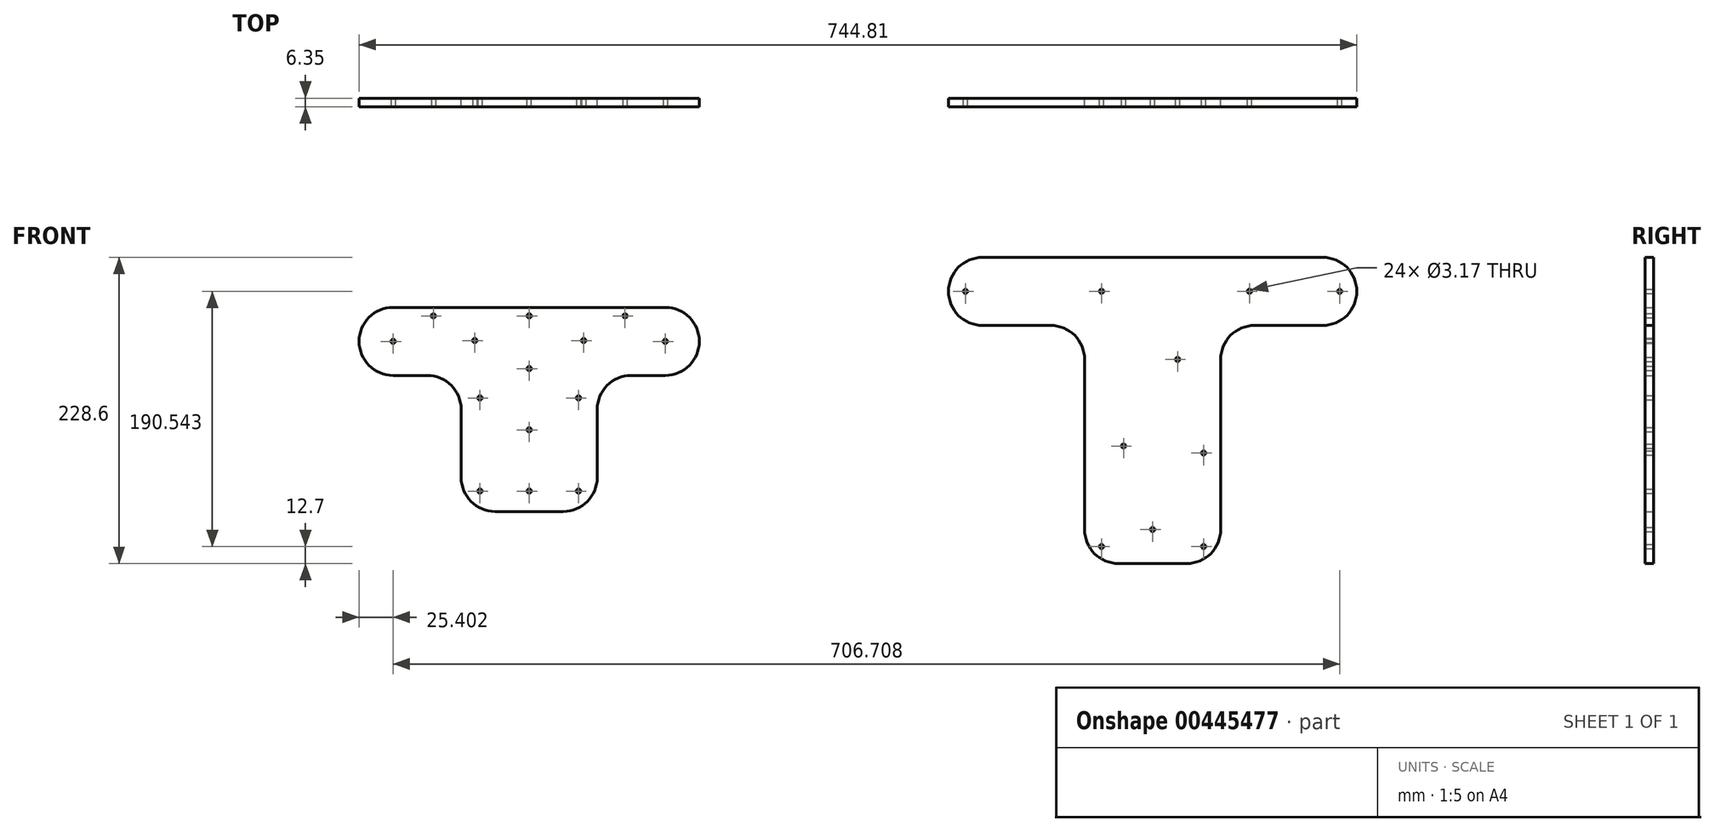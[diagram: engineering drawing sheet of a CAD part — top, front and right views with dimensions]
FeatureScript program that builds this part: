
annotation { "Feature Type Name" : "Feature", "Feature Type Description" : "" }
export const myFeature = defineFeature(function(context is Context, id is Id, definition is map)
    precondition{}
    {
        {
            var Q0;
            Q0=qCreatedBy(makeId("Front.planeOp"),FACE);
            var sketch = newSketch(context, id + "F0", { "sketchPlane" : qUnion([Q0])});
            skLineSegment(sketch, "E0.bottom", {"start": v(-50.8, 114.3) * mm, "end": v(50.8, 114.3) * mm});
            skLineSegment(sketch, "E0.top", {"start": v(-50.8, -114.3) * mm, "end": v(50.8, -114.3) * mm});
            skLineSegment(sketch, "E0.left", {"start": v(-50.8, 114.3) * mm, "end": v(-50.8, -114.3) * mm});
            skLineSegment(sketch, "E0.right", {"start": v(50.8, 114.3) * mm, "end": v(50.8, -114.3) * mm});
            skPoint(sketch, "E0.middle", {"position": v(0, 0) * mm});
            skCircle(sketch, "E1", {"center": v(0, -88.9) * mm, "radius": 15.24 * mm, "construction": true});
            skCircle(sketch, "E2", {"center": v(-21.7, -26.53) * mm, "radius": 50.8 * mm, "construction": true});
            skCircle(sketch, "E3", {"center": v(-21.7, -26.53) * mm, "radius": 25.4 * mm, "construction": true});
            skCircle(sketch, "E4", {"center": v(18.66, 38.1) * mm, "radius": 50.8 * mm, "construction": true});
            skCircle(sketch, "E5", {"center": v(18.66, 38.1) * mm, "radius": 25.4 * mm, "construction": true});
            skCircle(sketch, "E6", {"center": v(-38.1, 88.94) * mm, "radius": 50.8 * mm, "construction": true});
            skLineSegment(sketch, "E7", {"start": v(-50.8, 114.3) * mm, "end": v(-152.4, 114.3) * mm});
            skLineSegment(sketch, "E8", {"start": v(-152.4, 114.3) * mm, "end": v(-152.4, 63.5) * mm});
            skLineSegment(sketch, "E9", {"start": v(-152.4, 63.5) * mm, "end": v(-50.8, 63.5) * mm});
            skLineSegment(sketch, "E10", {"start": v(50.8, 63.5) * mm, "end": v(152.4, 63.5) * mm});
            skLineSegment(sketch, "E11", {"start": v(152.4, 63.5) * mm, "end": v(152.4, 114.3) * mm});
            skLineSegment(sketch, "E12", {"start": v(152.4, 114.3) * mm, "end": v(50.8, 114.3) * mm});
            skPoint(sketch, "E13", {"position": v(-152.4, 88.9) * mm});
            skCircle(sketch, "E14", {"center": v(-139.7, 88.9) * mm, "radius": 50.8 * mm, "construction": true});
            skLineSegment(sketch, "E15", {"start": v(-139.7, 88.9) * mm, "end": v(-152.4, 88.9) * mm});
            skLineSegment(sketch, "E16", {"start": v(152.4, 88.9) * mm, "end": v(139.7, 88.9) * mm});
            skPoint(sketch, "E16.endSnap0", {"position": v(152.4, 88.9) * mm});
            skCircle(sketch, "E17", {"center": v(139.7, 88.9) * mm, "radius": 50.8 * mm, "construction": true});
            skCircle(sketch, "E18", {"center": v(-139.7, 88.9) * mm, "radius": 1.59 * mm});
            skCircle(sketch, "E19", {"center": v(-38.1, 88.94) * mm, "radius": 1.59 * mm});
            skCircle(sketch, "E20", {"center": v(139.7, 88.9) * mm, "radius": 1.59 * mm});
            skCircle(sketch, "E21", {"center": v(18.66, 38.1) * mm, "radius": 1.59 * mm});
            skCircle(sketch, "E22", {"center": v(-21.7, -26.53) * mm, "radius": 1.59 * mm});
            skCircle(sketch, "E23", {"center": v(0, -88.9) * mm, "radius": 1.59 * mm});
            skLineSegment(sketch, "E24", {"start": v(-516.2, -75.44) * mm, "end": v(-414.6, -75.44) * mm});
            skLineSegment(sketch, "E25", {"start": v(-414.6, -75.44) * mm, "end": v(-414.6, 26.16) * mm});
            skLineSegment(sketch, "E26", {"start": v(-414.6, 26.16) * mm, "end": v(-338.4, 26.16) * mm});
            skLineSegment(sketch, "E27", {"start": v(-338.4, 26.16) * mm, "end": v(-338.4, 76.96) * mm});
            skLineSegment(sketch, "E28", {"start": v(-338.4, 76.96) * mm, "end": v(-592.4, 76.96) * mm});
            skLineSegment(sketch, "E29", {"start": v(-592.4, 76.96) * mm, "end": v(-592.4, 26.16) * mm});
            skLineSegment(sketch, "E30", {"start": v(-592.4, 26.16) * mm, "end": v(-516.2, 26.16) * mm});
            skLineSegment(sketch, "E31", {"start": v(-516.2, 26.16) * mm, "end": v(-516.2, -75.44) * mm});
            skCircle(sketch, "E32", {"center": v(-465.4, -60.2) * mm, "radius": 1.59 * mm});
            skPoint(sketch, "E32.centerSnap0", {"position": v(-465.4, -75.44) * mm});
            skLineSegment(sketch, "E33", {"start": v(-50.8, -114.3) * mm, "end": v(-38.1, -114.3) * mm});
            skLineSegment(sketch, "E34", {"start": v(-38.1, -114.3) * mm, "end": v(-38.1, -101.6) * mm});
            skCircle(sketch, "E35", {"center": v(-38.1, -101.6) * mm, "radius": 1.59 * mm});
            skLineSegment(sketch, "E36", {"start": v(50.8, -114.3) * mm, "end": v(38.1, -114.3) * mm});
            skLineSegment(sketch, "E37", {"start": v(38.1, -114.3) * mm, "end": v(38.1, -101.6) * mm});
            skCircle(sketch, "E38", {"center": v(38.1, -101.6) * mm, "radius": 1.59 * mm});
            skLineSegment(sketch, "E39", {"start": v(38.1, -31.75) * mm, "end": v(50.8, -31.75) * mm});
            skCircle(sketch, "E40", {"center": v(38.1, -31.75) * mm, "radius": 1.59 * mm});
            skLineSegment(sketch, "E41", {"start": v(-38.1, 88.94) * mm, "end": v(72.35, 88.94) * mm});
            skLineSegment(sketch, "E42", {"start": v(72.35, 88.94) * mm, "end": v(72.35, 114.3) * mm});
            skCircle(sketch, "E43", {"center": v(72.35, 88.94) * mm, "radius": 1.59 * mm});
            skSolve(sketch);
        }
        {
            var Q0;
            Q0 = qSketchRegion(id + "F0", true);
            extrude(context, id + "F1", {"entities" : qUnion([Q0]), "depth" : 6.35 * mm});
        }
        {
            var Q0;
            Q0=makeQuery(id+"F1.opExtrude","SWEPT_EDGE",EDGE,{"disambiguationData":[OSD([sQuery(id+"F0.wireOp",EDGE,"E0.left"),sQuery(id+"F0.wireOp",EDGE,"E9")])]});
            var Q1;
            Q1=makeQuery(id+"F1.opExtrude","SWEPT_EDGE",EDGE,{"disambiguationData":[OSD([sQuery(id+"F0.wireOp",EDGE,"E0.right"),sQuery(id+"F0.wireOp",EDGE,"E10")])]});
            var Q2;
            Q2=makeQuery(id+"F1.opExtrude","SWEPT_EDGE",EDGE,{"disambiguationData":[OSD([sQuery(id+"F0.wireOp",EDGE,"E10"),sQuery(id+"F0.wireOp",EDGE,"E11")])]});
            var Q3;
            Q3=makeQuery(id+"F1.opExtrude","SWEPT_EDGE",EDGE,{"disambiguationData":[OSD([sQuery(id+"F0.wireOp",EDGE,"E11"),sQuery(id+"F0.wireOp",EDGE,"E12")])]});
            var Q4;
            Q4=makeQuery(id+"F1.opExtrude","SWEPT_EDGE",EDGE,{"disambiguationData":[OSD([sQuery(id+"F0.wireOp",EDGE,"E0.top"),sQuery(id+"F0.wireOp",EDGE,"E0.right")])]});
            var Q5;
            Q5=makeQuery(id+"F1.opExtrude","SWEPT_EDGE",EDGE,{"disambiguationData":[OSD([sQuery(id+"F0.wireOp",EDGE,"E0.top"),sQuery(id+"F0.wireOp",EDGE,"E0.left")])]});
            var Q6;
            Q6=makeQuery(id+"F1.opExtrude","SWEPT_EDGE",EDGE,{"disambiguationData":[OSD([sQuery(id+"F0.wireOp",EDGE,"E8"),sQuery(id+"F0.wireOp",EDGE,"E9")])]});
            var Q7;
            Q7=makeQuery(id+"F1.opExtrude","SWEPT_EDGE",EDGE,{"disambiguationData":[OSD([sQuery(id+"F0.wireOp",EDGE,"E7"),sQuery(id+"F0.wireOp",EDGE,"E8")])]});
            fillet(context, id + "F2", {"entities" : qUnion([Q0, Q1, Q2, Q3, Q4, Q5, Q6, Q7]), "radius" : 25.4 * mm, "tangentPropagation" : true, "allowEdgeOverflow" : false});
        }
        {
            var Q0;
            Q0=makeQuery(id+"F1.opExtrude","SWEPT_EDGE",EDGE,{"disambiguationData":[OSD([sQuery(id+"F0.wireOp",EDGE,"E29"),sQuery(id+"F0.wireOp",EDGE,"E30")])]});
            var Q1;
            Q1=makeQuery(id+"F1.opExtrude","SWEPT_EDGE",EDGE,{"disambiguationData":[OSD([sQuery(id+"F0.wireOp",EDGE,"E30"),sQuery(id+"F0.wireOp",EDGE,"E31")])]});
            var Q2;
            Q2=makeQuery(id+"F1.opExtrude","SWEPT_EDGE",EDGE,{"disambiguationData":[OSD([sQuery(id+"F0.wireOp",EDGE,"E24"),sQuery(id+"F0.wireOp",EDGE,"E31")])]});
            var Q3;
            Q3=makeQuery(id+"F1.opExtrude","SWEPT_EDGE",EDGE,{"disambiguationData":[OSD([sQuery(id+"F0.wireOp",EDGE,"E25"),sQuery(id+"F0.wireOp",EDGE,"E26")])]});
            var Q4;
            Q4=makeQuery(id+"F1.opExtrude","SWEPT_EDGE",EDGE,{"disambiguationData":[OSD([sQuery(id+"F0.wireOp",EDGE,"E24"),sQuery(id+"F0.wireOp",EDGE,"E25")])]});
            var Q5;
            Q5=makeQuery(id+"F1.opExtrude","SWEPT_EDGE",EDGE,{"disambiguationData":[OSD([sQuery(id+"F0.wireOp",EDGE,"E27"),sQuery(id+"F0.wireOp",EDGE,"E28")])]});
            fillet(context, id + "F3", {"entities" : qUnion([Q0, Q1, Q2, Q3, Q4, Q5]), "radius" : 25.4 * mm, "tangentPropagation" : true, "allowEdgeOverflow" : false});
        }
        {
            var Q0;
            Q0=makeQuery(id+"F1.opExtrude","SWEPT_EDGE",EDGE,{"disambiguationData":[OSD([sQuery(id+"F0.wireOp",EDGE,"E26"),sQuery(id+"F0.wireOp",EDGE,"E27")])]});
            var Q1;
            Q1=makeQuery(id+"F1.opExtrude","SWEPT_EDGE",EDGE,{"disambiguationData":[OSD([sQuery(id+"F0.wireOp",EDGE,"E28"),sQuery(id+"F0.wireOp",EDGE,"E29")])]});
            fillet(context, id + "F4", {"entities" : qUnion([Q0, Q1]), "radius" : 25.4 * mm, "tangentPropagation" : true, "allowEdgeOverflow" : false});
        }
        {
            var Q0;
            Q0=makeQuery(id+"F1.opExtrude","CAP_FACE",FACE,{"disambiguationData":[OSD([sQuery(id+"F0.wireOp",EDGE,"E24"),sQuery(id+"F0.wireOp",EDGE,"E25"),sQuery(id+"F0.wireOp",EDGE,"E26"),sQuery(id+"F0.wireOp",EDGE,"E27"),sQuery(id+"F0.wireOp",EDGE,"E28"),sQuery(id+"F0.wireOp",EDGE,"E29"),sQuery(id+"F0.wireOp",EDGE,"E30"),sQuery(id+"F0.wireOp",EDGE,"E31"),sQuery(id+"F0.wireOp",EDGE,"E32")])],"isStart":false});
            var sketch = newSketch(context, id + "F5", { "sketchPlane" : qUnion([Q0])});
            skCircle(sketch, "E44", {"center": v(-465.4, -60.2) * mm, "radius": 15.24 * mm, "construction": true});
            skPoint(sketch, "E44.centerSnap0", {"position": v(-465.4, -75.44) * mm});
            skCircle(sketch, "E45", {"center": v(-465.4, -14.48) * mm, "radius": 30.48 * mm, "construction": true});
            skCircle(sketch, "E46", {"center": v(-465.4, -14.48) * mm, "radius": 15.24 * mm, "construction": true});
            skCircle(sketch, "E47", {"center": v(-465.4, 31.24) * mm, "radius": 30.48 * mm, "construction": true});
            skCircle(sketch, "E48", {"center": v(-465.4, 31.24) * mm, "radius": 15.24 * mm, "construction": true});
            skCircle(sketch, "E49", {"center": v(-506.05, 52.18) * mm, "radius": 30.48 * mm, "construction": true});
            skCircle(sketch, "E50", {"center": v(-363.8, 51.56) * mm, "radius": 30.48 * mm, "construction": true});
            skPoint(sketch, "E51.0", {"position": v(-338.4, 51.56) * mm});
            skCircle(sketch, "E52", {"center": v(-567, 51.56) * mm, "radius": 30.48 * mm, "construction": true});
            skCircle(sketch, "E53", {"center": v(-567, 51.56) * mm, "radius": 1.59 * mm});
            skCircle(sketch, "E54", {"center": v(-363.8, 104.22) * mm, "radius": 1.59 * mm});
            skCircle(sketch, "E55", {"center": v(-363.8, 51.56) * mm, "radius": 1.59 * mm});
            skCircle(sketch, "E56", {"center": v(-424.77, 52.18) * mm, "radius": 30.48 * mm, "construction": true});
            skCircle(sketch, "E57", {"center": v(-506.05, 52.18) * mm, "radius": 1.59 * mm});
            skCircle(sketch, "E58", {"center": v(-465.4, 31.24) * mm, "radius": 1.59 * mm});
            skCircle(sketch, "E59", {"center": v(-465.4, -14.48) * mm, "radius": 1.59 * mm});
            skCircle(sketch, "E60", {"center": v(-424.77, 52.18) * mm, "radius": 1.59 * mm});
            skCircle(sketch, "E61", {"center": v(-502.17, -60.2) * mm, "radius": 1.59 * mm});
            skArc(sketch, "E62.0", {"start": v(-516.2, -50.04) * mm, "mid": v(-508.77, -68) * mm, "end": v(-490.8, -75.44) * mm});
            skCircle(sketch, "E63", {"center": v(-428.65, -60.2) * mm, "radius": 1.59 * mm});
            skCircle(sketch, "E64", {"center": v(-428.65, 9.3) * mm, "radius": 1.59 * mm});
            skCircle(sketch, "E65", {"center": v(-502.17, 9.3) * mm, "radius": 1.59 * mm});
            skCircle(sketch, "E66", {"center": v(-465.4, 70.6) * mm, "radius": 1.59 * mm});
            skLineSegment(sketch, "E67", {"start": v(-550.16, 76.96) * mm, "end": v(-523.8, 76.96) * mm});
            skLineSegment(sketch, "E68", {"start": v(-523.8, 76.96) * mm, "end": v(-536.98, 76.96) * mm});
            skCircle(sketch, "E69", {"center": v(-536.98, 70.6) * mm, "radius": 1.59 * mm});
            skLineSegment(sketch, "E70", {"start": v(-406.4, 76.5) * mm, "end": v(-381.33, 76.5) * mm});
            skLineSegment(sketch, "E71", {"start": v(-381.33, 76.5) * mm, "end": v(-393.86, 76.5) * mm});
            skCircle(sketch, "E72", {"center": v(-393.86, 70.6) * mm, "radius": 1.59 * mm});
            skSolve(sketch);
        }
        {
            var Q0;
            Q0 = qSketchRegion(id + "F5", true);
            extrude(context, id + "F6", {"entities" : qUnion([Q0]), "operationType" : NewBodyOperationType.REMOVE, "oppositeDirection" : true, "depth" : 25.4 * mm, "offsetDistance" : 25.4 * mm});
        }
    });
